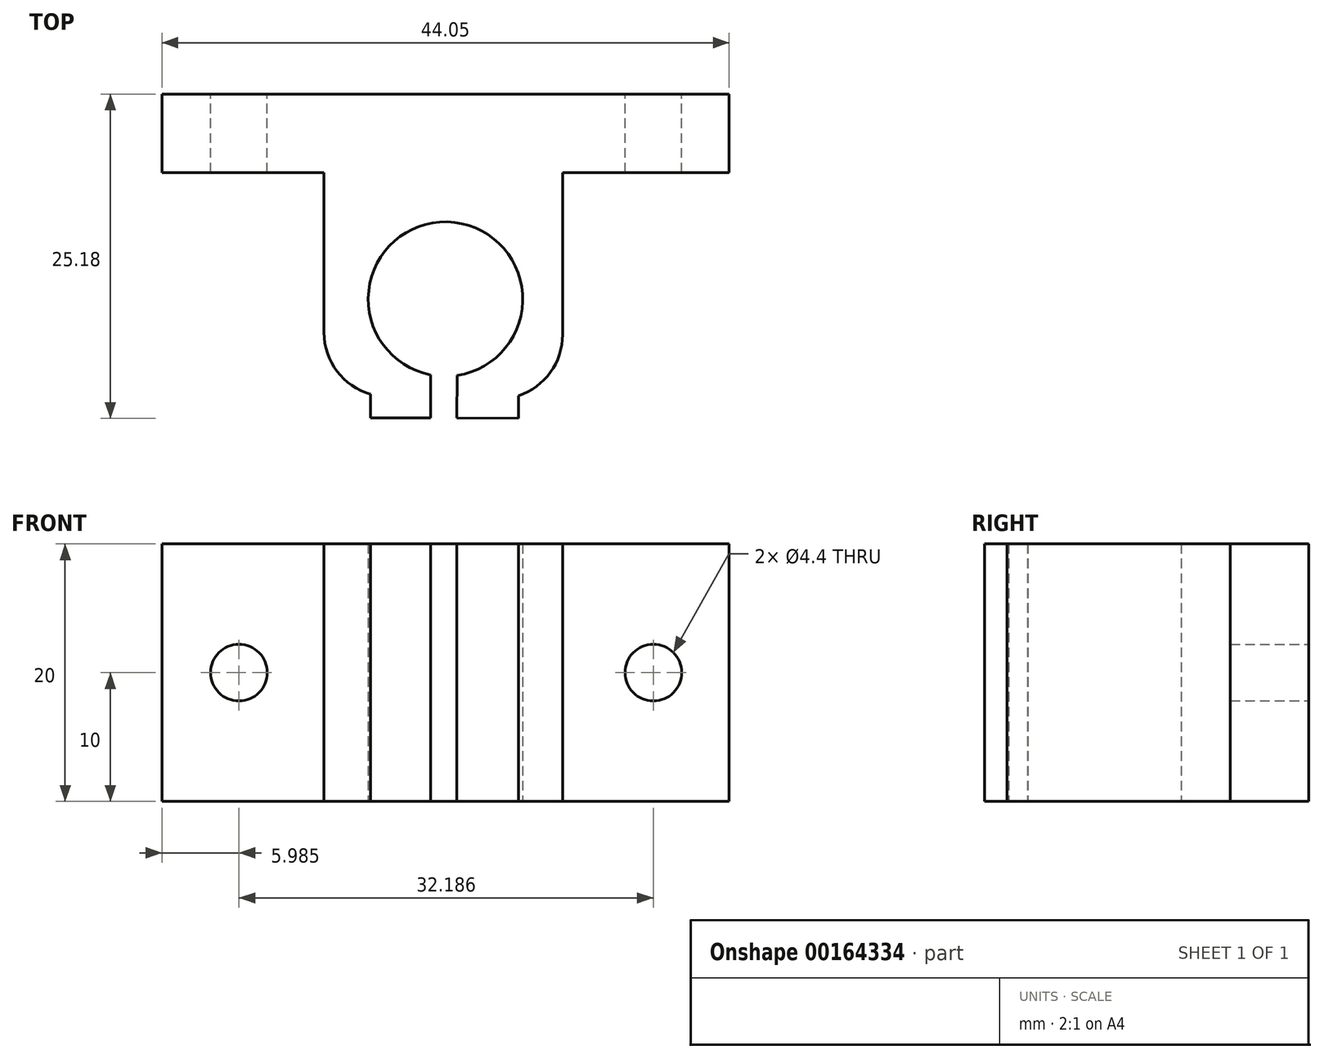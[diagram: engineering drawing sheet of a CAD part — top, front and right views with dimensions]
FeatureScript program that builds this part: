
annotation { "Feature Type Name" : "Feature", "Feature Type Description" : "" }
export const myFeature = defineFeature(function(context is Context, id is Id, definition is map)
    precondition{}
    {
        {
            var Q0;
            Q0=qCreatedBy(makeId("Top.planeOp"),FACE);
            var sketch = newSketch(context, id + "F0", { "sketchPlane" : qUnion([Q0])});
            skLineSegment(sketch, "E0", {"start": v(-25.59, 10.7) * mm, "end": v(18.46, 10.7) * mm});
            skLineSegment(sketch, "E1", {"start": v(18.46, 10.7) * mm, "end": v(18.46, 4.6) * mm});
            skLineSegment(sketch, "E2", {"start": v(18.46, 4.6) * mm, "end": v(5.54, 4.6) * mm});
            skLineSegment(sketch, "E3", {"start": v(5.54, 4.6) * mm, "end": v(5.54, -7.98) * mm});
            skLineSegment(sketch, "E4", {"start": v(-13, -7.82) * mm, "end": v(-13, 4.6) * mm});
            skLineSegment(sketch, "E5", {"start": v(-13, 4.6) * mm, "end": v(-25.59, 4.6) * mm});
            skLineSegment(sketch, "E6", {"start": v(-25.59, 4.6) * mm, "end": v(-25.59, 10.7) * mm});
            skPoint(sketch, "E7.visualSharp", {"position": v(-13, -11.73) * mm});
            skArc(sketch, "E7.filletArc", {"start": v(-13, -7.82) * mm, "mid": v(-11.99, -10.83) * mm, "end": v(-9.38, -12.63) * mm});
            skPoint(sketch, "E8.visualSharp", {"position": v(5.54, -11.73) * mm});
            skArc(sketch, "E8.filletArc", {"start": v(2.1, -12.73) * mm, "mid": v(4.59, -10.9) * mm, "end": v(5.54, -7.98) * mm});
            skArc(sketch, "E9", {"start": v(-2.67, -11.16) * mm, "mid": v(-3.43, 0.78) * mm, "end": v(-4.73, -11.1) * mm});
            skPoint(sketch, "E9.centerSnap0", {"position": v(-3.56, 10.7) * mm});
            skLineSegment(sketch, "E10", {"start": v(-9.38, -12.63) * mm, "end": v(-9.38, -14.45) * mm});
            skLineSegment(sketch, "E11", {"start": v(-9.38, -14.45) * mm, "end": v(-4.73, -14.45) * mm});
            skLineSegment(sketch, "E12", {"start": v(-4.73, -14.45) * mm, "end": v(-4.73, -11.1) * mm});
            skLineSegment(sketch, "E13", {"start": v(-2.67, -11.16) * mm, "end": v(-2.7, -14.45) * mm});
            skLineSegment(sketch, "E14", {"start": v(-2.7, -14.45) * mm, "end": v(2.1, -14.5) * mm});
            skLineSegment(sketch, "E15", {"start": v(2.1, -14.5) * mm, "end": v(2.1, -12.73) * mm});
            skSolve(sketch);
        }
        {
            var Q0;
            Q0 = qSketchRegion(id + "F0", true);
            extrude(context, id + "F1", {"entities" : qUnion([Q0]), "depth" : 20 * mm});
        }
        {
            var Q0;
            Q0=makeQuery(id+"F1.opExtrude","SWEPT_FACE",FACE,{"disambiguationData":[OSD([sQuery(id+"F0.wireOp",EDGE,"E0")])]});
            var sketch = newSketch(context, id + "F2", { "sketchPlane" : qUnion([Q0])});
            skCircle(sketch, "E16", {"center": v(-12.58, 10) * mm, "radius": 2.2 * mm});
            skPoint(sketch, "E16.centerSnap0", {"position": v(-18.46, 10) * mm});
            skCircle(sketch, "E17", {"center": v(19.6, 10) * mm, "radius": 2.2 * mm});
            skPoint(sketch, "E17.centerSnap0", {"position": v(25.59, 10) * mm});
            skSolve(sketch);
        }
        {
            var Q0;
            Q0 = qSketchRegion(id + "F2", true);
            extrude(context, id + "F3", {"entities" : qUnion([Q0]), "operationType" : NewBodyOperationType.REMOVE, "oppositeDirection" : true, "depth" : 25 * mm});
        }
    });
